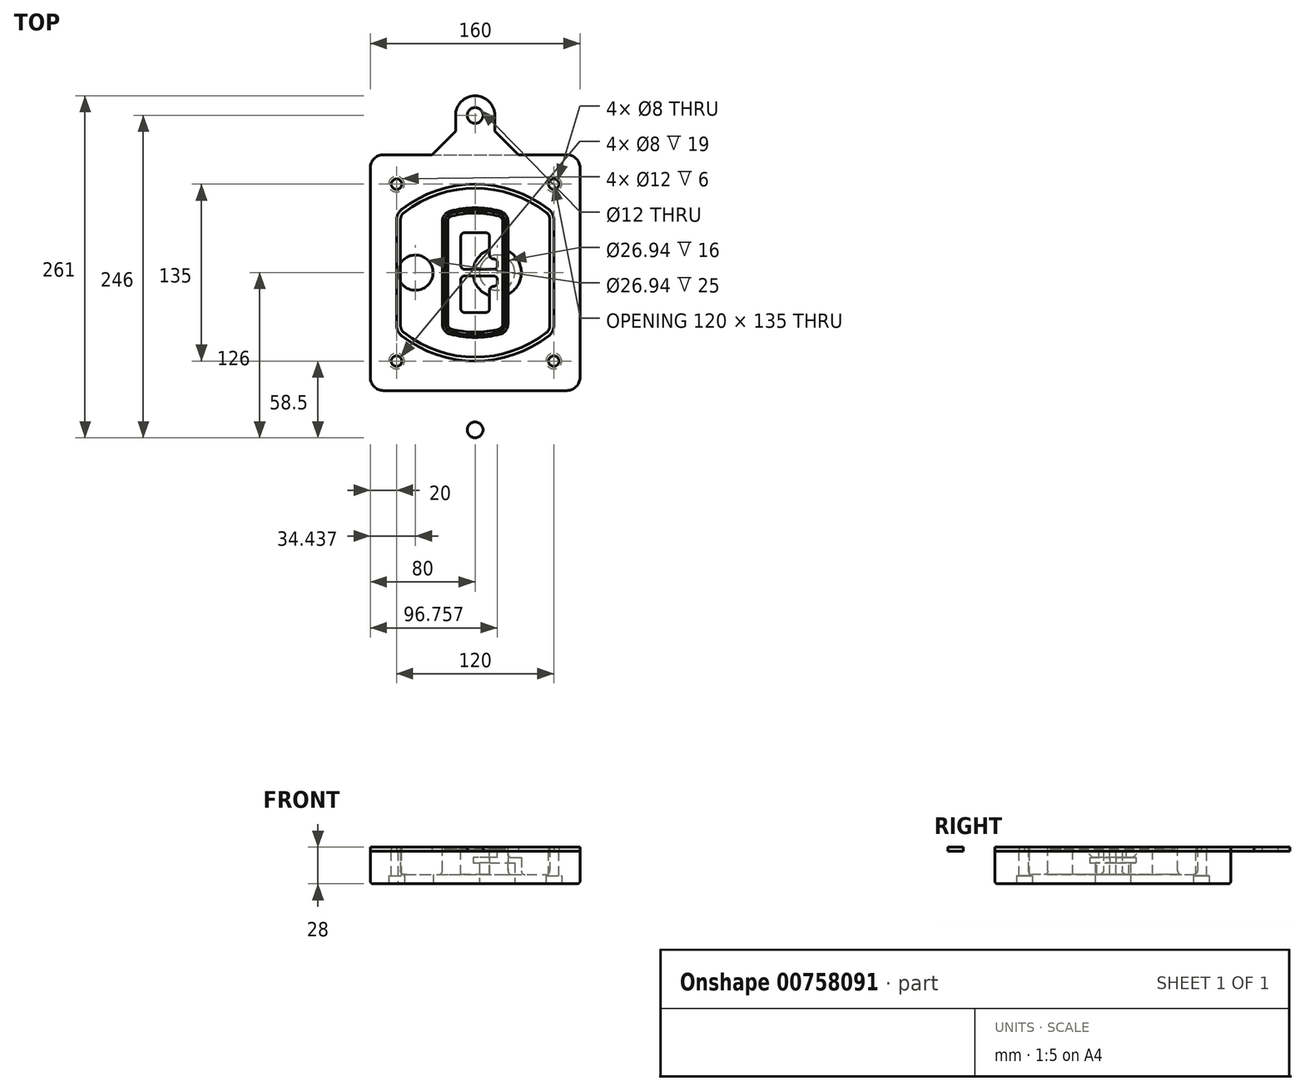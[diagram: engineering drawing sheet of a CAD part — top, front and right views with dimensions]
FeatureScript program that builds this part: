
annotation { "Feature Type Name" : "Feature", "Feature Type Description" : "" }
export const myFeature = defineFeature(function(context is Context, id is Id, definition is map)
    precondition{}
    {
        {
            var Q0;
            Q0=qCreatedBy(makeId("Top.planeOp"),FACE);
            var sketch = newSketch(context, id + "F0", { "sketchPlane" : qUnion([Q0])});
            skPoint(sketch, "E0.rect.middle", {"position": v(0, 0) * mm});
            skLineSegment(sketch, "E1.bottom", {"start": v(-70, -90) * mm, "end": v(70, -90) * mm});
            skLineSegment(sketch, "E1.top", {"start": v(-70, 90) * mm, "end": v(70, 90) * mm});
            skLineSegment(sketch, "E1.left", {"start": v(-80, -80) * mm, "end": v(-80, 80) * mm});
            skLineSegment(sketch, "E1.right", {"start": v(80, -80) * mm, "end": v(80, 80) * mm});
            skLineSegment(sketch, "E2", {"start": v(-80, 90) * mm, "end": v(80, -90) * mm, "construction": true});
            skLineSegment(sketch, "E3", {"start": v(80, 90) * mm, "end": v(-80, -90) * mm, "construction": true});
            skCircle(sketch, "E4", {"center": v(-60, 67.5) * mm, "radius": 4 * mm});
            skCircle(sketch, "E5", {"center": v(60, 67.5) * mm, "radius": 4 * mm});
            skCircle(sketch, "E6", {"center": v(60, -67.5) * mm, "radius": 4 * mm});
            skCircle(sketch, "E7", {"center": v(-60, -67.5) * mm, "radius": 4 * mm});
            skLineSegment(sketch, "E8", {"start": v(-60, 67.5) * mm, "end": v(60, 67.5) * mm, "construction": true});
            skLineSegment(sketch, "E9", {"start": v(60, 67.5) * mm, "end": v(60, -67.5) * mm, "construction": true});
            skLineSegment(sketch, "E10", {"start": v(60, -67.5) * mm, "end": v(-60, -67.5) * mm, "construction": true});
            skLineSegment(sketch, "E11", {"start": v(-60, -67.5) * mm, "end": v(-60, 67.5) * mm, "construction": true});
            skLineSegment(sketch, "E12", {"start": v(-60, 40.3) * mm, "end": v(-60, -40.3) * mm});
            skLineSegment(sketch, "E13", {"start": v(60, 40.3) * mm, "end": v(60, -40.3) * mm});
            skArc(sketch, "E14", {"start": v(56.15, 48.18) * mm, "mid": v(0, 67.5) * mm, "end": v(-56.15, 48.18) * mm});
            skArc(sketch, "E15", {"start": v(-56.15, -48.18) * mm, "mid": v(0, -67.5) * mm, "end": v(56.15, -48.18) * mm});
            skLineSegment(sketch, "E16", {"start": v(-60, 0) * mm, "end": v(60, 0) * mm, "construction": true});
            skPoint(sketch, "E17.visualSharp", {"position": v(-60, -45) * mm});
            skArc(sketch, "E17.filletArc", {"start": v(-60, -40.3) * mm, "mid": v(-58.99, -44.68) * mm, "end": v(-56.15, -48.18) * mm});
            skPoint(sketch, "E18.visualSharp", {"position": v(-60, 45) * mm});
            skArc(sketch, "E18.filletArc", {"start": v(-56.15, 48.18) * mm, "mid": v(-58.99, 44.68) * mm, "end": v(-60, 40.3) * mm});
            skPoint(sketch, "E19.visualSharp", {"position": v(60, 45) * mm});
            skArc(sketch, "E19.filletArc", {"start": v(60, 40.3) * mm, "mid": v(58.99, 44.68) * mm, "end": v(56.15, 48.18) * mm});
            skPoint(sketch, "E20.visualSharp", {"position": v(60, -45) * mm});
            skArc(sketch, "E20.filletArc", {"start": v(56.15, -48.18) * mm, "mid": v(58.99, -44.68) * mm, "end": v(60, -40.3) * mm});
            skPoint(sketch, "E21.visualSharp", {"position": v(-80, 90) * mm});
            skArc(sketch, "E21.filletArc", {"start": v(-70, 90) * mm, "mid": v(-77.07, 87.07) * mm, "end": v(-80, 80) * mm});
            skPoint(sketch, "E22.visualSharp", {"position": v(80, 90) * mm});
            skArc(sketch, "E22.filletArc", {"start": v(80, 80) * mm, "mid": v(77.07, 87.07) * mm, "end": v(70, 90) * mm});
            skPoint(sketch, "E23.visualSharp", {"position": v(80, -90) * mm});
            skArc(sketch, "E23.filletArc", {"start": v(70, -90) * mm, "mid": v(77.07, -87.07) * mm, "end": v(80, -80) * mm});
            skPoint(sketch, "E24.visualSharp", {"position": v(-80, -90) * mm});
            skArc(sketch, "E24.filletArc", {"start": v(-80, -80) * mm, "mid": v(-77.07, -87.07) * mm, "end": v(-70, -90) * mm});
            skArc(sketch, "E25.0", {"start": v(57, 40.3) * mm, "mid": v(56.3, 43.36) * mm, "end": v(54.3, 45.81) * mm});
            skLineSegment(sketch, "E25.1", {"start": v(57, 40.3) * mm, "end": v(57, -40.3) * mm});
            skArc(sketch, "E25.2", {"start": v(54.3, -45.81) * mm, "mid": v(56.3, -43.36) * mm, "end": v(57, -40.3) * mm});
            skArc(sketch, "E25.3", {"start": v(-54.3, -45.81) * mm, "mid": v(0, -64.5) * mm, "end": v(54.3, -45.81) * mm});
            skArc(sketch, "E25.4", {"start": v(-57, -40.3) * mm, "mid": v(-56.3, -43.36) * mm, "end": v(-54.3, -45.81) * mm});
            skArc(sketch, "E25.5", {"start": v(54.3, 45.81) * mm, "mid": v(0, 64.5) * mm, "end": v(-54.3, 45.81) * mm});
            skLineSegment(sketch, "E25.6", {"start": v(-57, 40.3) * mm, "end": v(-57, -40.3) * mm});
            skArc(sketch, "E25.7", {"start": v(-54.3, 45.81) * mm, "mid": v(-56.3, 43.36) * mm, "end": v(-57, 40.3) * mm});
            skArc(sketch, "E26.0", {"start": v(-58.62, 51.33) * mm, "mid": v(-62.58, 46.43) * mm, "end": v(-64, 40.3) * mm});
            skArc(sketch, "E26.1", {"start": v(58.62, 51.33) * mm, "mid": v(0, 71.5) * mm, "end": v(-58.62, 51.33) * mm});
            skArc(sketch, "E26.2", {"start": v(64, 40.3) * mm, "mid": v(62.58, 46.43) * mm, "end": v(58.62, 51.33) * mm});
            skLineSegment(sketch, "E26.3", {"start": v(64, 40.3) * mm, "end": v(64, -40.3) * mm});
            skArc(sketch, "E26.4", {"start": v(58.62, -51.33) * mm, "mid": v(62.58, -46.43) * mm, "end": v(64, -40.3) * mm});
            skLineSegment(sketch, "E26.5", {"start": v(-64, 40.3) * mm, "end": v(-64, -40.3) * mm});
            skArc(sketch, "E26.6", {"start": v(-58.62, -51.33) * mm, "mid": v(0, -71.5) * mm, "end": v(58.62, -51.33) * mm});
            skArc(sketch, "E26.7", {"start": v(-64, -40.3) * mm, "mid": v(-62.58, -46.43) * mm, "end": v(-58.62, -51.33) * mm});
            skSolve(sketch);
        }
        {
            var Q0;
            Q0=makeQuery(id+"F0.imprint","IMPRINT",FACE,{"disambiguationData":[TD([[makeQuery(id+"F0.imprint","IMPRINT",EDGE,{"derivedFrom":sQuery(id+"F0.wireOp",EDGE,"E1.bottom")}),1.0]])]});
            var Q1;
            Q1=makeQuery(id+"F0.imprint","IMPRINT",FACE,{"disambiguationData":[TD([[makeQuery(id+"F0.imprint","IMPRINT",EDGE,{"derivedFrom":sQuery(id+"F0.wireOp",EDGE,"E12")}),1.0]])]});
            var Q2;
            Q2=makeQuery(id+"F0.imprint","IMPRINT",FACE,{"disambiguationData":[TD([[makeQuery(id+"F0.imprint","IMPRINT",EDGE,{"derivedFrom":sQuery(id+"F0.wireOp",EDGE,"E25.0")}),1.0]])]});
            var Q3;
            Q3=makeQuery(id+"F0.imprint","IMPRINT",FACE,{"disambiguationData":[TD([[makeQuery(id+"F0.imprint","IMPRINT",EDGE,{"derivedFrom":sQuery(id+"F0.wireOp",EDGE,"E12")}),-1.0]])]});
            extrude(context, id + "F1", {"entities" : qUnion([Q0, Q1, Q2, Q3]), "oppositeDirection" : true, "depth" : 25 * mm, "offsetDistance" : 25 * mm});
        }
        {
            var Q0;
            Q0=makeQuery(id+"F0.imprint","IMPRINT",FACE,{"disambiguationData":[TD([[makeQuery(id+"F0.imprint","IMPRINT",EDGE,{"derivedFrom":sQuery(id+"F0.wireOp",EDGE,"E12")}),1.0]])]});
            extrude(context, id + "F2", {"entities" : qUnion([Q0]), "operationType" : NewBodyOperationType.ADD, "depth" : 3 * mm});
        }
        {
            var Q0;
            Q0=makeQuery(id+"F0.imprint","IMPRINT",FACE,{"disambiguationData":[TD([[makeQuery(id+"F0.imprint","IMPRINT",EDGE,{"derivedFrom":sQuery(id+"F0.wireOp",EDGE,"E25.0")}),1.0]])]});
            extrude(context, id + "F3", {"entities" : qUnion([Q0]), "operationType" : NewBodyOperationType.REMOVE, "oppositeDirection" : true, "depth" : 18 * mm});
        }
        {
            var Q0;
            Q0=makeQuery(id+"F2.opExtrude","CAP_FACE",FACE,{"disambiguationData":[OSD([sQuery(id+"F0.wireOp",EDGE,"E12"),sQuery(id+"F0.wireOp",EDGE,"E13"),sQuery(id+"F0.wireOp",EDGE,"E14"),sQuery(id+"F0.wireOp",EDGE,"E15"),sQuery(id+"F0.wireOp",EDGE,"E17.filletArc"),sQuery(id+"F0.wireOp",EDGE,"E18.filletArc"),sQuery(id+"F0.wireOp",EDGE,"E19.filletArc"),sQuery(id+"F0.wireOp",EDGE,"E20.filletArc"),sQuery(id+"F0.wireOp",EDGE,"E25.0"),sQuery(id+"F0.wireOp",EDGE,"E25.1"),sQuery(id+"F0.wireOp",EDGE,"E25.2"),sQuery(id+"F0.wireOp",EDGE,"E25.3"),sQuery(id+"F0.wireOp",EDGE,"E25.4"),sQuery(id+"F0.wireOp",EDGE,"E25.5"),sQuery(id+"F0.wireOp",EDGE,"E25.6"),sQuery(id+"F0.wireOp",EDGE,"E25.7")])],"isStart":false});
            var sketch = newSketch(context, id + "F4", { "sketchPlane" : qUnion([Q0])});
            skArc(sketch, "E27.0", {"start": v(-19.08, -46.97) * mm, "mid": v(0, -49.5) * mm, "end": v(19.08, -46.97) * mm});
            skArc(sketch, "E28.0", {"start": v(19.08, 46.97) * mm, "mid": v(0, 49.5) * mm, "end": v(-19.08, 46.97) * mm});
            skLineSegment(sketch, "E29", {"start": v(-25, 39.25) * mm, "end": v(-25, -39.25) * mm});
            skLineSegment(sketch, "E30", {"start": v(25, 39.25) * mm, "end": v(25, -39.25) * mm});
            skLineSegment(sketch, "E31", {"start": v(-25, 45.1) * mm, "end": v(25, 45.1) * mm, "construction": true});
            skLineSegment(sketch, "E32", {"start": v(-25, -45.1) * mm, "end": v(25, -45.1) * mm, "construction": true});
            skPoint(sketch, "E33.visualSharp", {"position": v(-25, 45.1) * mm});
            skArc(sketch, "E33.filletArc", {"start": v(-19.08, 46.97) * mm, "mid": v(-23.35, 44.11) * mm, "end": v(-25, 39.25) * mm});
            skPoint(sketch, "E34.visualSharp", {"position": v(25, 45.1) * mm});
            skArc(sketch, "E34.filletArc", {"start": v(25, 39.25) * mm, "mid": v(23.35, 44.11) * mm, "end": v(19.08, 46.97) * mm});
            skPoint(sketch, "E35.visualSharp", {"position": v(25, -45.1) * mm});
            skArc(sketch, "E35.filletArc", {"start": v(19.08, -46.97) * mm, "mid": v(23.35, -44.11) * mm, "end": v(25, -39.25) * mm});
            skPoint(sketch, "E36.visualSharp", {"position": v(-25, -45.1) * mm});
            skArc(sketch, "E36.filletArc", {"start": v(-25, -39.25) * mm, "mid": v(-23.35, -44.11) * mm, "end": v(-19.08, -46.97) * mm});
            skArc(sketch, "E37.0", {"start": v(54.3, 45.81) * mm, "mid": v(0, 64.5) * mm, "end": v(-54.3, 45.81) * mm});
            skArc(sketch, "E37.1", {"start": v(-54.3, 45.81) * mm, "mid": v(-56.3, 43.36) * mm, "end": v(-57, 40.3) * mm});
            skLineSegment(sketch, "E37.2", {"start": v(-57, 40.3) * mm, "end": v(-57, -40.3) * mm});
            skArc(sketch, "E37.3", {"start": v(-57, -40.3) * mm, "mid": v(-56.3, -43.36) * mm, "end": v(-54.3, -45.81) * mm});
            skArc(sketch, "E37.4", {"start": v(-54.3, -45.81) * mm, "mid": v(0, -64.5) * mm, "end": v(54.3, -45.81) * mm});
            skArc(sketch, "E37.5", {"start": v(54.3, -45.81) * mm, "mid": v(56.3, -43.36) * mm, "end": v(57, -40.3) * mm});
            skLineSegment(sketch, "E37.6", {"start": v(57, 40.3) * mm, "end": v(57, -40.3) * mm});
            skArc(sketch, "E37.7", {"start": v(57, 40.3) * mm, "mid": v(56.3, 43.36) * mm, "end": v(54.3, 45.81) * mm});
            skLineSegment(sketch, "E38.0", {"start": v(23, 39.25) * mm, "end": v(23, -39.25) * mm});
            skArc(sketch, "E38.1", {"start": v(18.56, -45.04) * mm, "mid": v(21.76, -42.9) * mm, "end": v(23, -39.25) * mm});
            skArc(sketch, "E38.2", {"start": v(-18.56, -45.04) * mm, "mid": v(0, -47.5) * mm, "end": v(18.56, -45.04) * mm});
            skArc(sketch, "E38.3", {"start": v(-23, -39.25) * mm, "mid": v(-21.76, -42.9) * mm, "end": v(-18.56, -45.04) * mm});
            skLineSegment(sketch, "E38.4", {"start": v(-23, 39.25) * mm, "end": v(-23, -39.25) * mm});
            skArc(sketch, "E38.5", {"start": v(23, 39.25) * mm, "mid": v(21.76, 42.9) * mm, "end": v(18.56, 45.04) * mm});
            skArc(sketch, "E38.6", {"start": v(-18.56, 45.04) * mm, "mid": v(-21.76, 42.9) * mm, "end": v(-23, 39.25) * mm});
            skArc(sketch, "E38.7", {"start": v(18.56, 45.04) * mm, "mid": v(0, 47.5) * mm, "end": v(-18.56, 45.04) * mm});
            skArc(sketch, "E39.0", {"start": v(21, 39.25) * mm, "mid": v(20.18, 41.68) * mm, "end": v(18.04, 43.1) * mm});
            skLineSegment(sketch, "E39.1", {"start": v(21, 39.25) * mm, "end": v(21, -39.25) * mm});
            skArc(sketch, "E39.2", {"start": v(18.04, -43.1) * mm, "mid": v(20.18, -41.68) * mm, "end": v(21, -39.25) * mm});
            skArc(sketch, "E39.3", {"start": v(-18.04, -43.1) * mm, "mid": v(0, -45.5) * mm, "end": v(18.04, -43.1) * mm});
            skArc(sketch, "E39.4", {"start": v(-21, -39.25) * mm, "mid": v(-20.18, -41.68) * mm, "end": v(-18.04, -43.1) * mm});
            skArc(sketch, "E39.5", {"start": v(18.04, 43.1) * mm, "mid": v(0, 45.5) * mm, "end": v(-18.04, 43.1) * mm});
            skLineSegment(sketch, "E39.6", {"start": v(-21, 39.25) * mm, "end": v(-21, -39.25) * mm});
            skArc(sketch, "E39.7", {"start": v(-18.04, 43.1) * mm, "mid": v(-20.18, 41.68) * mm, "end": v(-21, 39.25) * mm});
            skLineSegment(sketch, "E40", {"start": v(-25, 0) * mm, "end": v(25, 0) * mm, "construction": true});
            skLineSegment(sketch, "E41", {"start": v(-11, 5.5) * mm, "end": v(-11, 27.5) * mm});
            skLineSegment(sketch, "E42", {"start": v(-8, 30.5) * mm, "end": v(8, 30.5) * mm});
            skLineSegment(sketch, "E43", {"start": v(11, 27.5) * mm, "end": v(11, 13.5) * mm});
            skLineSegment(sketch, "E44", {"start": v(14, 10.5) * mm, "end": v(14, 10.5) * mm});
            skLineSegment(sketch, "E45", {"start": v(17, 7.5) * mm, "end": v(17, 5.5) * mm});
            skLineSegment(sketch, "E46", {"start": v(14, 2.5) * mm, "end": v(-8, 2.5) * mm});
            skPoint(sketch, "E47.visualSharp", {"position": v(-11, 30.5) * mm});
            skArc(sketch, "E47.filletArc", {"start": v(-8, 30.5) * mm, "mid": v(-10.12, 29.62) * mm, "end": v(-11, 27.5) * mm});
            skPoint(sketch, "E48.visualSharp", {"position": v(11, 30.5) * mm});
            skArc(sketch, "E48.filletArc", {"start": v(11, 27.5) * mm, "mid": v(10.12, 29.62) * mm, "end": v(8, 30.5) * mm});
            skPoint(sketch, "E49.visualSharp", {"position": v(11, 10.5) * mm});
            skArc(sketch, "E49.filletArc", {"start": v(11, 13.5) * mm, "mid": v(11.88, 11.38) * mm, "end": v(14, 10.5) * mm});
            skPoint(sketch, "E50.visualSharp", {"position": v(17, 10.5) * mm});
            skArc(sketch, "E50.filletArc", {"start": v(17, 7.5) * mm, "mid": v(16.12, 9.62) * mm, "end": v(14, 10.5) * mm});
            skPoint(sketch, "E51.visualSharp", {"position": v(17, 2.5) * mm});
            skArc(sketch, "E51.filletArc", {"start": v(14, 2.5) * mm, "mid": v(16.12, 3.38) * mm, "end": v(17, 5.5) * mm});
            skPoint(sketch, "E52.visualSharp", {"position": v(-11, 2.5) * mm});
            skArc(sketch, "E52.filletArc", {"start": v(-11, 5.5) * mm, "mid": v(-10.12, 3.38) * mm, "end": v(-8, 2.5) * mm});
            skLineSegment(sketch, "E53.0.MirrorCS", {"start": v(14, -2.5) * mm, "end": v(-8, -2.5) * mm});
            skArc(sketch, "E54.0.MirrorCS", {"start": v(-11, -5.5) * mm, "mid": v(-10.12, -3.38) * mm, "end": v(-8, -2.5) * mm});
            skLineSegment(sketch, "E55.0.MirrorCS", {"start": v(-11, -5.5) * mm, "end": v(-11, -27.5) * mm});
            skArc(sketch, "E56.0.MirrorCS", {"start": v(-8, -30.5) * mm, "mid": v(-10.12, -29.62) * mm, "end": v(-11, -27.5) * mm});
            skLineSegment(sketch, "E57.0.MirrorCS", {"start": v(-8, -30.5) * mm, "end": v(8, -30.5) * mm});
            skArc(sketch, "E58.0.MirrorCS", {"start": v(11, -27.5) * mm, "mid": v(10.12, -29.62) * mm, "end": v(8, -30.5) * mm});
            skLineSegment(sketch, "E59.0.MirrorCS", {"start": v(11, -27.5) * mm, "end": v(11, -13.5) * mm});
            skArc(sketch, "E60.0.MirrorCS", {"start": v(11, -13.5) * mm, "mid": v(11.88, -11.38) * mm, "end": v(14, -10.5) * mm});
            skArc(sketch, "E61.0.MirrorCS", {"start": v(17, -7.5) * mm, "mid": v(16.12, -9.62) * mm, "end": v(14, -10.5) * mm});
            skLineSegment(sketch, "E62.0.MirrorCS", {"start": v(17, -7.5) * mm, "end": v(17, -5.5) * mm});
            skArc(sketch, "E63.0.MirrorCS", {"start": v(14, -2.5) * mm, "mid": v(16.12, -3.38) * mm, "end": v(17, -5.5) * mm});
            skSolve(sketch);
        }
        {
            var Q0;
            Q0=makeQuery(id+"F4.imprint","IMPRINT",FACE,{"disambiguationData":[TD([[makeQuery(id+"F4.imprint","IMPRINT",EDGE,{"derivedFrom":sQuery(id+"F4.wireOp",EDGE,"E27.0")}),1.0]])]});
            var Q1;
            Q1=makeQuery(id+"F4.imprint","IMPRINT",FACE,{"disambiguationData":[TD([[makeQuery(id+"F4.imprint","IMPRINT",EDGE,{"derivedFrom":sQuery(id+"F4.wireOp",EDGE,"E38.0")}),-1.0]])]});
            var Q2;
            Q2=makeQuery(id+"F4.imprint","IMPRINT",FACE,{"disambiguationData":[TD([[makeQuery(id+"F4.imprint","IMPRINT",EDGE,{"derivedFrom":sQuery(id+"F4.wireOp",EDGE,"E39.0")}),1.0]])]});
            extrude(context, id + "F5", {"entities" : qUnion([Q0, Q1, Q2]), "operationType" : NewBodyOperationType.ADD, "endBound" : BoundingType.UP_TO_NEXT, "oppositeDirection" : true, "depth" : 25 * mm});
        }
        {
            var Q0;
            Q0=makeQuery(id+"F4.imprint","IMPRINT",FACE,{"disambiguationData":[TD([[makeQuery(id+"F4.imprint","IMPRINT",EDGE,{"derivedFrom":sQuery(id+"F4.wireOp",EDGE,"E38.0")}),-1.0]])]});
            extrude(context, id + "F6", {"entities" : qUnion([Q0]), "operationType" : NewBodyOperationType.REMOVE, "oppositeDirection" : true, "depth" : 2 * mm});
        }
        {
            var Q0;
            Q0=makeQuery(id+"F1.opExtrude","CAP_FACE",FACE,{"disambiguationData":[OSD([sQuery(id+"F0.wireOp",EDGE,"E1.bottom"),sQuery(id+"F0.wireOp",EDGE,"E1.top"),sQuery(id+"F0.wireOp",EDGE,"E1.left"),sQuery(id+"F0.wireOp",EDGE,"E1.right"),sQuery(id+"F0.wireOp",EDGE,"E4"),sQuery(id+"F0.wireOp",EDGE,"E5"),sQuery(id+"F0.wireOp",EDGE,"E6"),sQuery(id+"F0.wireOp",EDGE,"E7"),sQuery(id+"F0.wireOp",EDGE,"E21.filletArc"),sQuery(id+"F0.wireOp",EDGE,"E22.filletArc"),sQuery(id+"F0.wireOp",EDGE,"E23.filletArc"),sQuery(id+"F0.wireOp",EDGE,"E24.filletArc")])],"isStart":false});
            var sketch = newSketch(context, id + "F7", { "sketchPlane" : qUnion([Q0])});
            skCircle(sketch, "E64", {"center": v(16.76, 0) * mm, "radius": 13.47 * mm});
            skCircle(sketch, "E65", {"center": v(-45.56, 0) * mm, "radius": 13.47 * mm});
            skLineSegment(sketch, "E66", {"start": v(80, 0) * mm, "end": v(-80, 0) * mm});
            skCircle(sketch, "E67", {"center": v(16.76, 0) * mm, "radius": 18.47 * mm});
            skCircle(sketch, "E68", {"center": v(60, -67.5) * mm, "radius": 6 * mm});
            skCircle(sketch, "E69", {"center": v(-60, -67.5) * mm, "radius": 6 * mm});
            skCircle(sketch, "E70", {"center": v(-60, 67.5) * mm, "radius": 6 * mm});
            skCircle(sketch, "E71", {"center": v(60, 67.5) * mm, "radius": 6 * mm});
            skSolve(sketch);
        }
        {
            var Q0;
            {var subQ1=sQuery(id+"F7.wireOp",EDGE,"E66");var subQ4=sQuery(id+"F7.wireOp",EDGE,"E64");var subQ6=makeQuery(id+"F7.imprint","INTERSECT",VERTEX,{"disambiguationData":[OD(0.0)],"derivedFrom":[subQ4,subQ1]});Q0=makeQuery(id+"F7.imprint","IMPRINT",FACE,{"disambiguationData":[TD([[makeQuery(id+"F7.imprint","IMPRINT",EDGE,{"disambiguationData":[TD([[subQ6,-1.0]])],"derivedFrom":subQ4}),-1.0]])]});}
            var Q1;
            {var subQ0=sQuery(id+"F7.wireOp",EDGE,"E66");var subQ1=sQuery(id+"F7.wireOp",EDGE,"E64");var subQ3=makeQuery(id+"F7.imprint","INTERSECT",VERTEX,{"disambiguationData":[OD(0.0)],"derivedFrom":[subQ1,subQ0]});Q1=makeQuery(id+"F7.imprint","IMPRINT",FACE,{"disambiguationData":[TD([[makeQuery(id+"F7.imprint","IMPRINT",EDGE,{"disambiguationData":[TD([[subQ3,-1.0]])],"derivedFrom":subQ1}),1.0]])]});}
            var Q2;
            {var subQ0=sQuery(id+"F7.wireOp",EDGE,"E66");var subQ1=sQuery(id+"F7.wireOp",EDGE,"E64");var subQ3=makeQuery(id+"F7.imprint","INTERSECT",VERTEX,{"disambiguationData":[OD(0.0)],"derivedFrom":[subQ1,subQ0]});Q2=makeQuery(id+"F7.imprint","IMPRINT",FACE,{"disambiguationData":[TD([[makeQuery(id+"F7.imprint","IMPRINT",EDGE,{"disambiguationData":[TD([[subQ3,1.0]])],"derivedFrom":subQ1}),1.0]])]});}
            var Q3;
            {var subQ1=sQuery(id+"F7.wireOp",EDGE,"E66");var subQ4=sQuery(id+"F7.wireOp",EDGE,"E64");var subQ6=makeQuery(id+"F7.imprint","INTERSECT",VERTEX,{"disambiguationData":[OD(0.0)],"derivedFrom":[subQ4,subQ1]});Q3=makeQuery(id+"F7.imprint","IMPRINT",FACE,{"disambiguationData":[TD([[makeQuery(id+"F7.imprint","IMPRINT",EDGE,{"disambiguationData":[TD([[subQ6,1.0]])],"derivedFrom":subQ4}),-1.0]])]});}
            extrude(context, id + "F8", {"entities" : qUnion([Q0, Q1, Q2, Q3]), "operationType" : NewBodyOperationType.ADD, "oppositeDirection" : true, "depth" : 20 * mm});
        }
        {
            var Q0;
            {var subQ0=sQuery(id+"F7.wireOp",EDGE,"E66");var subQ1=sQuery(id+"F7.wireOp",EDGE,"E64");var subQ3=makeQuery(id+"F7.imprint","INTERSECT",VERTEX,{"disambiguationData":[OD(0.0)],"derivedFrom":[subQ1,subQ0]});Q0=makeQuery(id+"F7.imprint","IMPRINT",FACE,{"disambiguationData":[TD([[makeQuery(id+"F7.imprint","IMPRINT",EDGE,{"disambiguationData":[TD([[subQ3,-1.0]])],"derivedFrom":subQ1}),1.0]])]});}
            var Q1;
            {var subQ0=sQuery(id+"F7.wireOp",EDGE,"E66");var subQ1=sQuery(id+"F7.wireOp",EDGE,"E64");var subQ3=makeQuery(id+"F7.imprint","INTERSECT",VERTEX,{"disambiguationData":[OD(0.0)],"derivedFrom":[subQ1,subQ0]});Q1=makeQuery(id+"F7.imprint","IMPRINT",FACE,{"disambiguationData":[TD([[makeQuery(id+"F7.imprint","IMPRINT",EDGE,{"disambiguationData":[TD([[subQ3,1.0]])],"derivedFrom":subQ1}),1.0]])]});}
            extrude(context, id + "F9", {"entities" : qUnion([Q0, Q1]), "operationType" : NewBodyOperationType.REMOVE, "oppositeDirection" : true, "depth" : 16 * mm});
        }
        {
            var Q0;
            {var subQ0=sQuery(id+"F7.wireOp",EDGE,"E66");var subQ1=sQuery(id+"F7.wireOp",EDGE,"E65");var subQ3=makeQuery(id+"F7.imprint","INTERSECT",VERTEX,{"disambiguationData":[OD(0.0)],"derivedFrom":[subQ1,subQ0]});Q0=makeQuery(id+"F7.imprint","IMPRINT",FACE,{"disambiguationData":[TD([[makeQuery(id+"F7.imprint","IMPRINT",EDGE,{"disambiguationData":[TD([[subQ3,-1.0]])],"derivedFrom":subQ1}),1.0]])]});}
            var Q1;
            {var subQ0=sQuery(id+"F7.wireOp",EDGE,"E66");var subQ1=sQuery(id+"F7.wireOp",EDGE,"E65");var subQ3=makeQuery(id+"F7.imprint","INTERSECT",VERTEX,{"disambiguationData":[OD(0.0)],"derivedFrom":[subQ1,subQ0]});Q1=makeQuery(id+"F7.imprint","IMPRINT",FACE,{"disambiguationData":[TD([[makeQuery(id+"F7.imprint","IMPRINT",EDGE,{"disambiguationData":[TD([[subQ3,1.0]])],"derivedFrom":subQ1}),1.0]])]});}
            extrude(context, id + "F10", {"entities" : qUnion([Q0, Q1]), "operationType" : NewBodyOperationType.REMOVE, "oppositeDirection" : true, "depth" : 25 * mm});
        }
        {
            var Q0;
            Q0=makeQuery(id+"F7.imprint","IMPRINT",FACE,{"disambiguationData":[TD([[makeQuery(id+"F7.imprint","IMPRINT",EDGE,{"derivedFrom":sQuery(id+"F7.wireOp",EDGE,"E68")}),1.0]])]});
            var Q1;
            Q1=makeQuery(id+"F7.imprint","IMPRINT",FACE,{"disambiguationData":[TD([[makeQuery(id+"F7.imprint","IMPRINT",EDGE,{"derivedFrom":makeQuery(id+"F1.opExtrude","CAP_EDGE",EDGE,{"disambiguationData":[OSD([sQuery(id+"F0.wireOp",EDGE,"E5")])],"isStart":false})}),-1.0]])]});
            var Q2;
            Q2=makeQuery(id+"F7.imprint","IMPRINT",FACE,{"disambiguationData":[TD([[makeQuery(id+"F7.imprint","IMPRINT",EDGE,{"derivedFrom":sQuery(id+"F7.wireOp",EDGE,"E69")}),1.0]])]});
            var Q3;
            Q3=makeQuery(id+"F7.imprint","IMPRINT",FACE,{"disambiguationData":[TD([[makeQuery(id+"F7.imprint","IMPRINT",EDGE,{"derivedFrom":makeQuery(id+"F1.opExtrude","CAP_EDGE",EDGE,{"disambiguationData":[OSD([sQuery(id+"F0.wireOp",EDGE,"E4")])],"isStart":false})}),-1.0]])]});
            var Q4;
            Q4=makeQuery(id+"F7.imprint","IMPRINT",FACE,{"disambiguationData":[TD([[makeQuery(id+"F7.imprint","IMPRINT",EDGE,{"derivedFrom":sQuery(id+"F7.wireOp",EDGE,"E70")}),1.0]])]});
            var Q5;
            Q5=makeQuery(id+"F7.imprint","IMPRINT",FACE,{"disambiguationData":[TD([[makeQuery(id+"F7.imprint","IMPRINT",EDGE,{"derivedFrom":makeQuery(id+"F1.opExtrude","CAP_EDGE",EDGE,{"disambiguationData":[OSD([sQuery(id+"F0.wireOp",EDGE,"E7")])],"isStart":false})}),-1.0]])]});
            var Q6;
            Q6=makeQuery(id+"F7.imprint","IMPRINT",FACE,{"disambiguationData":[TD([[makeQuery(id+"F7.imprint","IMPRINT",EDGE,{"derivedFrom":sQuery(id+"F7.wireOp",EDGE,"E71")}),1.0]])]});
            var Q7;
            Q7=makeQuery(id+"F7.imprint","IMPRINT",FACE,{"disambiguationData":[TD([[makeQuery(id+"F7.imprint","IMPRINT",EDGE,{"derivedFrom":makeQuery(id+"F1.opExtrude","CAP_EDGE",EDGE,{"disambiguationData":[OSD([sQuery(id+"F0.wireOp",EDGE,"E6")])],"isStart":false})}),-1.0]])]});
            extrude(context, id + "F11", {"entities" : qUnion([Q0, Q1, Q2, Q3, Q4, Q5, Q6, Q7]), "operationType" : NewBodyOperationType.REMOVE, "oppositeDirection" : true, "depth" : 6 * mm});
        }
        {
            var Q0;
            Q0=makeQuery(id+"F9.boolean.opBoolean","COPY",FACE,{"derivedFrom":makeQuery(id+"F9.opExtrude","CAP_FACE",FACE,{"disambiguationData":[OSD([sQuery(id+"F7.wireOp",EDGE,"E64")])],"isStart":false})});
            var sketch = newSketch(context, id + "F12", { "sketchPlane" : qUnion([Q0])});
            skArc(sketch, "E72.0", {"start": v(11, 17.55) * mm, "mid": v(2.57, 11.82) * mm, "end": v(-1.54, 2.5) * mm});
            skArc(sketch, "E72.1", {"start": v(-1.54, -2.5) * mm, "mid": v(2.57, -11.82) * mm, "end": v(11, -17.55) * mm});
            skLineSegment(sketch, "E73", {"start": v(-1.54, -2.5) * mm, "end": v(14, -2.5) * mm});
            skLineSegment(sketch, "E74.0", {"start": v(14, 2.5) * mm, "end": v(-1.54, 2.5) * mm});
            skArc(sketch, "E74.1", {"start": v(14, 2.5) * mm, "mid": v(16.12, 3.38) * mm, "end": v(17, 5.5) * mm});
            skLineSegment(sketch, "E74.2", {"start": v(17, 7.5) * mm, "end": v(17, 5.5) * mm});
            skArc(sketch, "E74.3", {"start": v(17, 7.5) * mm, "mid": v(16.12, 9.62) * mm, "end": v(14, 10.5) * mm});
            skArc(sketch, "E74.4", {"start": v(11, 13.5) * mm, "mid": v(11.88, 11.38) * mm, "end": v(14, 10.5) * mm});
            skLineSegment(sketch, "E74.5", {"start": v(11, 17.55) * mm, "end": v(11, 13.5) * mm});
            skLineSegment(sketch, "E74.7", {"start": v(14, -2.5) * mm, "end": v(-1.54, -2.5) * mm});
            skArc(sketch, "E74.8", {"start": v(14, -2.5) * mm, "mid": v(16.12, -3.38) * mm, "end": v(17, -5.5) * mm});
            skLineSegment(sketch, "E74.9", {"start": v(17, -7.5) * mm, "end": v(17, -5.5) * mm});
            skArc(sketch, "E74.10", {"start": v(17, -7.5) * mm, "mid": v(16.12, -9.62) * mm, "end": v(14, -10.5) * mm});
            skArc(sketch, "E74.11", {"start": v(11, -13.5) * mm, "mid": v(11.88, -11.38) * mm, "end": v(14, -10.5) * mm});
            skLineSegment(sketch, "E74.12", {"start": v(11, -17.55) * mm, "end": v(11, -13.5) * mm});
            skPoint(sketch, "E75.orphan", {"position": v(11, -27.5) * mm});
            skPoint(sketch, "E76.orphan", {"position": v(-8, -2.5) * mm});
            skPoint(sketch, "E77.orphan", {"position": v(-8, 2.5) * mm});
            skPoint(sketch, "E78.orphan", {"position": v(11, 27.5) * mm});
            skSolve(sketch);
        }
        {
            var Q0;
            {var subQ7=sQuery(id+"F12.wireOp",EDGE,"E72.0");var subQ14=sQuery(id+"F12.wireOp",EDGE,"E72.1");var subQ16=sQuery(id+"F12.wireOp",EDGE,"E74.1");var subQ18=sQuery(id+"F12.wireOp",EDGE,"E74.8");Q0=qUnion([makeQuery(id+"F12.imprint","IMPRINT",FACE,{"disambiguationData":[TD([[makeQuery(id+"F12.imprint","IMPRINT",EDGE,{"derivedFrom":subQ7}),1.0]])]}),makeQuery(id+"F12.imprint","IMPRINT",FACE,{"disambiguationData":[TD([[makeQuery(id+"F12.imprint","IMPRINT",EDGE,{"derivedFrom":subQ14}),1.0]])]}),makeQuery(id+"F12.imprint","IMPRINT",FACE,{"disambiguationData":[TD([[makeQuery(id+"F12.imprint","IMPRINT",EDGE,{"derivedFrom":subQ16}),1.0]])]}),makeQuery(id+"F12.imprint","IMPRINT",FACE,{"disambiguationData":[TD([[makeQuery(id+"F12.imprint","IMPRINT",EDGE,{"derivedFrom":subQ18}),-1.0]])]})]);}
            var Q1;
            Q1=makeQuery(id+"F5.boolean.opBoolean","SPLIT",FACE,{"disambiguationData":[TD([makeQuery(id+"F5.opExtrude","SWEPT_FACE",FACE,{"disambiguationData":[OSD([sQuery(id+"F4.wireOp",EDGE,"E41")])]})])],"derivedFrom":makeQuery(id+"F3.boolean.opBoolean","COPY",FACE,{"derivedFrom":makeQuery(id+"F3.opExtrude","CAP_FACE",FACE,{"disambiguationData":[OSD([sQuery(id+"F0.wireOp",EDGE,"E25.0"),sQuery(id+"F0.wireOp",EDGE,"E25.1"),sQuery(id+"F0.wireOp",EDGE,"E25.2"),sQuery(id+"F0.wireOp",EDGE,"E25.3"),sQuery(id+"F0.wireOp",EDGE,"E25.4"),sQuery(id+"F0.wireOp",EDGE,"E25.5"),sQuery(id+"F0.wireOp",EDGE,"E25.6"),sQuery(id+"F0.wireOp",EDGE,"E25.7")])],"isStart":false})})});
            extrude(context, id + "F13", {"entities" : qUnion([Q0]), "operationType" : NewBodyOperationType.REMOVE, "endBound" : BoundingType.UP_TO_SURFACE, "endBoundEntityFace" : qUnion([Q1]), "depth" : 25 * mm});
        }
        {
            var Q0;
            Q0=makeQuery(id+"F3.boolean.opBoolean","COPY",EDGE,{"derivedFrom":makeQuery(id+"F3.opExtrude","CAP_EDGE",EDGE,{"disambiguationData":[OSD([sQuery(id+"F0.wireOp",EDGE,"E25.6")])],"isStart":false})});
            var Q1;
            Q1=makeQuery(id+"F8.boolean.opBoolean","INTERSECT",EDGE,{"derivedFrom":[makeQuery(id+"F5.opExtrude","SWEPT_FACE",FACE,{"disambiguationData":[OSD([sQuery(id+"F4.wireOp",EDGE,"E30")])]}),makeQuery(id+"F8.opExtrude","CAP_FACE",FACE,{"disambiguationData":[OSD([sQuery(id+"F7.wireOp",EDGE,"E67")])],"isStart":false})]});
            var Q2;
            Q2=makeQuery(id+"F8.boolean.opBoolean","INTERSECT",EDGE,{"disambiguationData":[OD(1.0)],"derivedFrom":[makeQuery(id+"F5.opExtrude","SWEPT_FACE",FACE,{"disambiguationData":[OSD([sQuery(id+"F4.wireOp",EDGE,"E30")])]}),makeQuery(id+"F8.opExtrude","SWEPT_FACE",FACE,{"disambiguationData":[OSD([sQuery(id+"F7.wireOp",EDGE,"E67")])]})]});
            var Q3;
            {var subQ0=sQuery(id+"F4.wireOp",EDGE,"E30");Q3=makeQuery(id+"F8.boolean.opBoolean","SPLIT",EDGE,{"disambiguationData":[TD([makeQuery(id+"F5.opExtrude","SWEPT_FACE",FACE,{"disambiguationData":[OSD([sQuery(id+"F4.wireOp",EDGE,"E35.filletArc")])]})])],"derivedFrom":makeQuery(id+"F5.opExtrude","CAP_EDGE",EDGE,{"disambiguationData":[OSD([subQ0])],"isStart":false})});}
            var Q4;
            {var subQ0=sQuery(id+"F0.wireOp",EDGE,"E25.7");var subQ1=sQuery(id+"F0.wireOp",EDGE,"E25.1");var subQ2=sQuery(id+"F0.wireOp",EDGE,"E25.6");var subQ3=sQuery(id+"F0.wireOp",EDGE,"E25.5");var subQ4=sQuery(id+"F0.wireOp",EDGE,"E25.4");var subQ5=sQuery(id+"F0.wireOp",EDGE,"E25.0");var subQ6=sQuery(id+"F0.wireOp",EDGE,"E25.2");var subQ7=sQuery(id+"F0.wireOp",EDGE,"E25.3");Q4=makeQuery(id+"F8.boolean.opBoolean","INTERSECT",EDGE,{"derivedFrom":[makeQuery(id+"F5.boolean.opBoolean","SPLIT",FACE,{"disambiguationData":[TD([makeQuery(id+"F2.opExtrude","SWEPT_FACE",FACE,{"disambiguationData":[OSD([subQ5])]})])],"derivedFrom":makeQuery(id+"F3.boolean.opBoolean","COPY",FACE,{"derivedFrom":makeQuery(id+"F3.opExtrude","CAP_FACE",FACE,{"disambiguationData":[OSD([subQ5,subQ1,subQ6,subQ7,subQ4,subQ3,subQ2,subQ0])],"isStart":false})})}),makeQuery(id+"F8.opExtrude","SWEPT_FACE",FACE,{"disambiguationData":[OSD([sQuery(id+"F7.wireOp",EDGE,"E67")])]})]});}
            var Q5;
            Q5=makeQuery(id+"F8.boolean.opBoolean","INTERSECT",EDGE,{"disambiguationData":[OD(0.0)],"derivedFrom":[makeQuery(id+"F5.opExtrude","SWEPT_FACE",FACE,{"disambiguationData":[OSD([sQuery(id+"F4.wireOp",EDGE,"E30")])]}),makeQuery(id+"F8.opExtrude","SWEPT_FACE",FACE,{"disambiguationData":[OSD([sQuery(id+"F7.wireOp",EDGE,"E67")])]})]});
            fillet(context, id + "F14", {"entities" : qUnion([Q0, Q1, Q2, Q3, Q4, Q5]), "radius" : 3 * mm, "tangentPropagation" : true, "allowEdgeOverflow" : false});
        }
        {
            var Q0;
            Q0=makeQuery(id+"F1.opExtrude","CAP_EDGE",EDGE,{"disambiguationData":[OSD([sQuery(id+"F0.wireOp",EDGE,"E1.bottom")])],"isStart":false});
            fillet(context, id + "F15", {"entities" : qUnion([Q0]), "radius" : 2 * mm, "tangentPropagation" : true, "allowEdgeOverflow" : false});
        }
        {
            var Q0;
            {var subQ0=sQuery(id+"F0.wireOp",EDGE,"E21.filletArc");var subQ1=sQuery(id+"F0.wireOp",EDGE,"E7");var subQ2=sQuery(id+"F0.wireOp",EDGE,"E6");var subQ3=sQuery(id+"F0.wireOp",EDGE,"E5");var subQ4=sQuery(id+"F0.wireOp",EDGE,"E4");var subQ5=sQuery(id+"F0.wireOp",EDGE,"E22.filletArc");var subQ6=sQuery(id+"F0.wireOp",EDGE,"E1.bottom");var subQ7=sQuery(id+"F0.wireOp",EDGE,"E1.right");var subQ8=sQuery(id+"F0.wireOp",EDGE,"E1.top");var subQ9=sQuery(id+"F0.wireOp",EDGE,"E1.left");var subQ10=sQuery(id+"F0.wireOp",EDGE,"E23.filletArc");var subQ11=sQuery(id+"F0.wireOp",EDGE,"E24.filletArc");Q0=makeQuery(id+"F2.boolean.opBoolean","SPLIT",FACE,{"disambiguationData":[TD([makeQuery(id+"F1.opExtrude","SWEPT_FACE",FACE,{"disambiguationData":[OSD([subQ6])]})])],"derivedFrom":makeQuery(id+"F1.opExtrude","CAP_FACE",FACE,{"disambiguationData":[OSD([subQ6,subQ8,subQ9,subQ7,subQ4,subQ3,subQ2,subQ1,subQ0,subQ5,subQ10,subQ11])],"isStart":true})});}
            var sketch = newSketch(context, id + "F16", { "sketchPlane" : qUnion([Q0])});
            skLineSegment(sketch, "E79.0", {"start": v(-70, 90) * mm, "end": v(70, 90) * mm});
            skArc(sketch, "E79.1", {"start": v(-70, 90) * mm, "mid": v(-77.07, 87.07) * mm, "end": v(-80, 80) * mm});
            skLineSegment(sketch, "E79.2", {"start": v(-80, -80) * mm, "end": v(-80, 80) * mm});
            skArc(sketch, "E79.3", {"start": v(-80, -80) * mm, "mid": v(-77.07, -87.07) * mm, "end": v(-70, -90) * mm});
            skLineSegment(sketch, "E79.4", {"start": v(-70, -90) * mm, "end": v(70, -90) * mm});
            skArc(sketch, "E79.5", {"start": v(70, -90) * mm, "mid": v(77.07, -87.07) * mm, "end": v(80, -80) * mm});
            skLineSegment(sketch, "E79.6", {"start": v(80, -80) * mm, "end": v(80, 80) * mm});
            skArc(sketch, "E79.7", {"start": v(80, 80) * mm, "mid": v(77.07, 87.07) * mm, "end": v(70, 90) * mm});
            skCircle(sketch, "E79.8", {"center": v(60, 67.5) * mm, "radius": 4 * mm});
            skCircle(sketch, "E79.9", {"center": v(-60, 67.5) * mm, "radius": 4 * mm});
            skCircle(sketch, "E79.10", {"center": v(-60, -67.5) * mm, "radius": 4 * mm});
            skCircle(sketch, "E79.11", {"center": v(60, -67.5) * mm, "radius": 4 * mm});
            skArc(sketch, "E79.12", {"start": v(56.15, 48.18) * mm, "mid": v(0, 67.5) * mm, "end": v(-56.15, 48.18) * mm});
            skArc(sketch, "E79.13", {"start": v(-56.15, 48.18) * mm, "mid": v(-58.99, 44.68) * mm, "end": v(-60, 40.3) * mm});
            skLineSegment(sketch, "E79.14", {"start": v(-60, 40.3) * mm, "end": v(-60, -40.3) * mm});
            skArc(sketch, "E79.15", {"start": v(-60, -40.3) * mm, "mid": v(-58.99, -44.68) * mm, "end": v(-56.15, -48.18) * mm});
            skArc(sketch, "E79.16", {"start": v(-56.15, -48.18) * mm, "mid": v(0, -67.5) * mm, "end": v(56.15, -48.18) * mm});
            skArc(sketch, "E79.17", {"start": v(56.15, -48.18) * mm, "mid": v(58.99, -44.68) * mm, "end": v(60, -40.3) * mm});
            skLineSegment(sketch, "E79.18", {"start": v(60, 40.3) * mm, "end": v(60, -40.3) * mm});
            skArc(sketch, "E79.19", {"start": v(60, 40.3) * mm, "mid": v(58.99, 44.68) * mm, "end": v(56.15, 48.18) * mm});
            skLineSegment(sketch, "E80", {"start": v(-33, 90) * mm, "end": v(-15, 108) * mm});
            skLineSegment(sketch, "E81", {"start": v(33, 90) * mm, "end": v(15, 108) * mm});
            skLineSegment(sketch, "E82", {"start": v(15, 108) * mm, "end": v(15, 120) * mm});
            skLineSegment(sketch, "E83", {"start": v(-15, 108) * mm, "end": v(-15, 120) * mm});
            skArc(sketch, "E84", {"start": v(15, 120) * mm, "mid": v(0, 135) * mm, "end": v(-15, 120) * mm});
            skCircle(sketch, "E85", {"center": v(0, 120) * mm, "radius": 6 * mm});
            skLineSegment(sketch, "E86", {"start": v(0, 120) * mm, "end": v(0, 90) * mm, "construction": true});
            skLineSegment(sketch, "E87", {"start": v(-60, 0) * mm, "end": v(80, 0) * mm, "construction": true});
            skLineSegment(sketch, "E88.MirrorCS", {"start": v(33, -90) * mm, "end": v(15, -108) * mm});
            skLineSegment(sketch, "E89.MirrorCS", {"start": v(15, -108) * mm, "end": v(15, -120) * mm});
            skLineSegment(sketch, "E90.MirrorCS", {"start": v(0, -120) * mm, "end": v(0, -90) * mm, "construction": true});
            skCircle(sketch, "E91.MirrorC", {"center": v(0, -120) * mm, "radius": 6 * mm});
            skLineSegment(sketch, "E92.MirrorCS", {"start": v(-33, -90) * mm, "end": v(-15, -108) * mm});
            skArc(sketch, "E93.MirrorCS", {"start": v(15, -120) * mm, "mid": v(0, -135) * mm, "end": v(-15, -120) * mm});
            skLineSegment(sketch, "E94.MirrorCS", {"start": v(-15, -108) * mm, "end": v(-15, -120) * mm});
            skSolve(sketch);
        }
        {
            var Q0;
            {var subQ1=sQuery(id+"F16.wireOp",EDGE,"E80");Q0=makeQuery(id+"F16.imprint","IMPRINT",FACE,{"disambiguationData":[TD([[makeQuery(id+"F16.imprint","IMPRINT",EDGE,{"derivedFrom":subQ1}),-1.0]])]});}
            var Q1;
            {var subQ1=sQuery(id+"F16.wireOp",EDGE,"E79.1");Q1=makeQuery(id+"F16.imprint","IMPRINT",FACE,{"disambiguationData":[TD([[makeQuery(id+"F16.imprint","IMPRINT",EDGE,{"derivedFrom":subQ1}),1.0]])]});}
            var Q2;
            Q2=makeQuery(id+"F16.imprint","IMPRINT",FACE,{"disambiguationData":[TD([[makeQuery(id+"F16.imprint","IMPRINT",EDGE,{"derivedFrom":sQuery(id+"F16.wireOp",EDGE,"E91.MirrorC")}),1.0]])]});
            var Q3;
            Q3=makeQuery(id+"F2.opExtrude","CAP_FACE",FACE,{"disambiguationData":[OSD([sQuery(id+"F0.wireOp",EDGE,"E12"),sQuery(id+"F0.wireOp",EDGE,"E13"),sQuery(id+"F0.wireOp",EDGE,"E14"),sQuery(id+"F0.wireOp",EDGE,"E15"),sQuery(id+"F0.wireOp",EDGE,"E17.filletArc"),sQuery(id+"F0.wireOp",EDGE,"E18.filletArc"),sQuery(id+"F0.wireOp",EDGE,"E19.filletArc"),sQuery(id+"F0.wireOp",EDGE,"E20.filletArc"),sQuery(id+"F0.wireOp",EDGE,"E25.0"),sQuery(id+"F0.wireOp",EDGE,"E25.1"),sQuery(id+"F0.wireOp",EDGE,"E25.2"),sQuery(id+"F0.wireOp",EDGE,"E25.3"),sQuery(id+"F0.wireOp",EDGE,"E25.4"),sQuery(id+"F0.wireOp",EDGE,"E25.5"),sQuery(id+"F0.wireOp",EDGE,"E25.6"),sQuery(id+"F0.wireOp",EDGE,"E25.7")])],"isStart":false});
            extrude(context, id + "F17", {"entities" : qUnion([Q0, Q1, Q2]), "endBound" : BoundingType.UP_TO_SURFACE, "depth" : 180 * mm, "endBoundEntityFace" : qUnion([Q3]), "offsetDistance" : 25 * mm});
        }
    });
